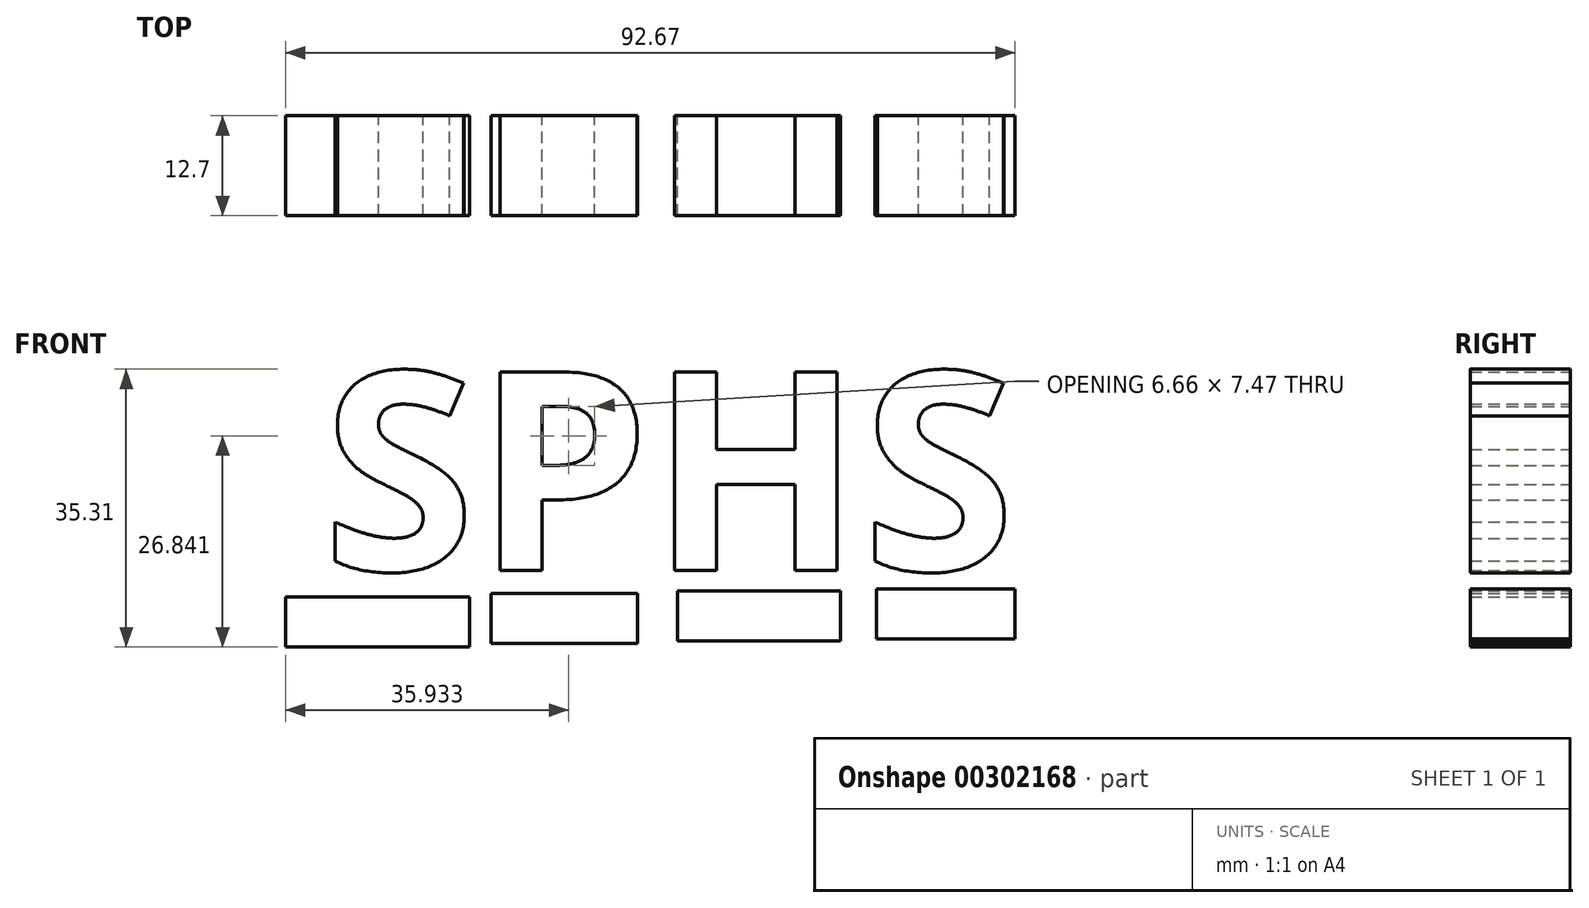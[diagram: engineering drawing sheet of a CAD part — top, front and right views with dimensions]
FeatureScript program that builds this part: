
annotation { "Feature Type Name" : "Feature", "Feature Type Description" : "" }
export const myFeature = defineFeature(function(context is Context, id is Id, definition is map)
    precondition{}
    {
        {
            var Q0;
            Q0=qCreatedBy(makeId("Front.planeOp"),FACE);
            var sketch = newSketch(context, id + "F0", { "sketchPlane" : qUnion([Q0])});
            skText(sketch, "E0", { "text": "SPHS", "fontName": "OpenSans-Bold.ttf"});
            const initialGuessF0  = {"E0": [-0.03028, -0.00855, 1, 0, 0.0254]};
            skSetInitialGuess(sketch, initialGuessF0);
            skSolve(sketch);
        }
        {
            var Q0;
            Q0 = qSketchRegion(id + "F0", true);
            extrude(context, id + "F1", {"entities" : qUnion([Q0]), "depth" : 12.7 * mm});
        }
        {
            var Q0;
            Q0=qCreatedBy(makeId("Front.planeOp"),FACE);
            var sketch = newSketch(context, id + "F2", { "sketchPlane" : qUnion([Q0])});
            skLineSegment(sketch, "E1.bottom", {"start": v(-34.94, -11.97) * mm, "end": v(-11.58, -11.97) * mm});
            skLineSegment(sketch, "E1.top", {"start": v(-34.94, -18.32) * mm, "end": v(-11.58, -18.32) * mm});
            skLineSegment(sketch, "E1.left", {"start": v(-34.94, -11.97) * mm, "end": v(-34.94, -18.32) * mm});
            skLineSegment(sketch, "E1.right", {"start": v(-11.58, -11.97) * mm, "end": v(-11.58, -18.32) * mm});
            skSolve(sketch);
        }
        {
            var Q0;
            Q0=qCreatedBy(makeId("Front.planeOp"),FACE);
            var sketch = newSketch(context, id + "F3", { "sketchPlane" : qUnion([Q0])});
            skLineSegment(sketch, "E2.bottom", {"start": v(-8.83, -11.53) * mm, "end": v(9.8, -11.53) * mm});
            skLineSegment(sketch, "E2.top", {"start": v(-8.83, -17.88) * mm, "end": v(9.8, -17.88) * mm});
            skLineSegment(sketch, "E2.left", {"start": v(-8.83, -11.53) * mm, "end": v(-8.83, -17.88) * mm});
            skLineSegment(sketch, "E2.right", {"start": v(9.8, -11.53) * mm, "end": v(9.8, -17.88) * mm});
            skSolve(sketch);
        }
        {
            var Q0;
            Q0=qCreatedBy(makeId("Front.planeOp"),FACE);
            var sketch = newSketch(context, id + "F4", { "sketchPlane" : qUnion([Q0])});
            skLineSegment(sketch, "E3.bottom", {"start": v(14.84, -11.16) * mm, "end": v(35.53, -11.16) * mm});
            skLineSegment(sketch, "E3.top", {"start": v(14.84, -17.51) * mm, "end": v(35.53, -17.51) * mm});
            skLineSegment(sketch, "E3.left", {"start": v(14.84, -11.16) * mm, "end": v(14.84, -17.51) * mm});
            skLineSegment(sketch, "E3.right", {"start": v(35.53, -11.16) * mm, "end": v(35.53, -17.51) * mm});
            skSolve(sketch);
        }
        {
            var Q0;
            Q0=qCreatedBy(makeId("Front.planeOp"),FACE);
            var sketch = newSketch(context, id + "F5", { "sketchPlane" : qUnion([Q0])});
            skLineSegment(sketch, "E4.bottom", {"start": v(40.11, -10.92) * mm, "end": v(57.73, -10.92) * mm});
            skLineSegment(sketch, "E4.top", {"start": v(40.11, -17.27) * mm, "end": v(57.73, -17.27) * mm});
            skLineSegment(sketch, "E4.left", {"start": v(40.11, -10.92) * mm, "end": v(40.11, -17.27) * mm});
            skLineSegment(sketch, "E4.right", {"start": v(57.73, -10.92) * mm, "end": v(57.73, -17.27) * mm});
            skSolve(sketch);
        }
        {
            var Q0;
            Q0=makeQuery(id+"F2.imprint","IMPRINT",FACE,{"disambiguationData":[TD([[makeQuery(id+"F2.imprint","IMPRINT",EDGE,{"derivedFrom":sQuery(id+"F2.wireOp",EDGE,"E1.bottom")}),-1.0]])]});
            extrude(context, id + "F6", {"entities" : qUnion([Q0]), "depth" : 12.7 * mm});
        }
        {
            var Q0;
            Q0=makeQuery(id+"F3.imprint","IMPRINT",FACE,{"disambiguationData":[TD([[makeQuery(id+"F3.imprint","IMPRINT",EDGE,{"derivedFrom":sQuery(id+"F3.wireOp",EDGE,"E2.bottom")}),-1.0]])]});
            extrude(context, id + "F7", {"entities" : qUnion([Q0]), "depth" : 12.7 * mm});
        }
        {
            var Q0;
            Q0=makeQuery(id+"F4.imprint","IMPRINT",FACE,{"disambiguationData":[TD([[makeQuery(id+"F4.imprint","IMPRINT",EDGE,{"derivedFrom":sQuery(id+"F4.wireOp",EDGE,"E3.bottom")}),-1.0]])]});
            extrude(context, id + "F8", {"entities" : qUnion([Q0]), "depth" : 12.7 * mm});
        }
        {
            var Q0;
            Q0=makeQuery(id+"F5.imprint","IMPRINT",FACE,{"disambiguationData":[TD([[makeQuery(id+"F5.imprint","IMPRINT",EDGE,{"derivedFrom":sQuery(id+"F5.wireOp",EDGE,"E4.bottom")}),-1.0]])]});
            extrude(context, id + "F9", {"entities" : qUnion([Q0]), "depth" : 12.7 * mm});
        }
    });
